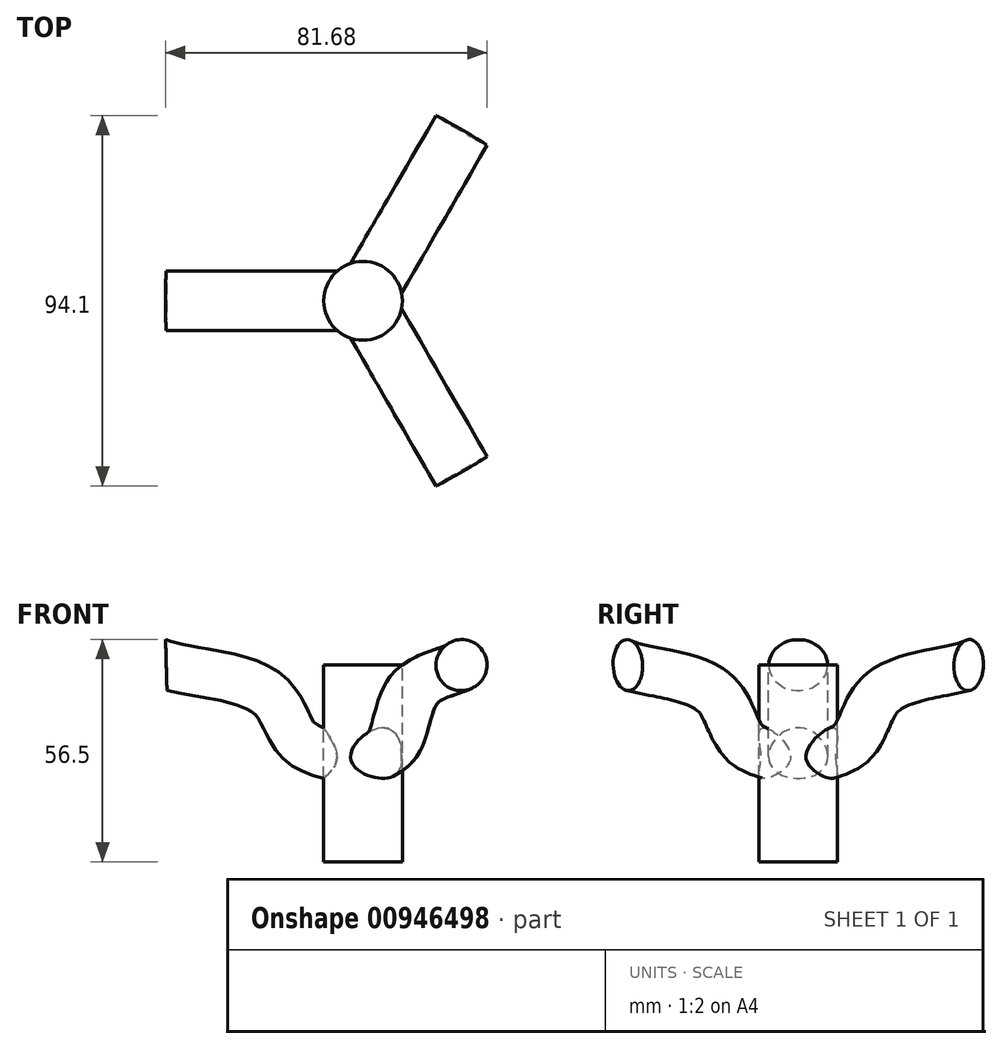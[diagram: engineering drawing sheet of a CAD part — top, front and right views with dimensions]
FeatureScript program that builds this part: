
annotation { "Feature Type Name" : "Feature", "Feature Type Description" : "" }
export const myFeature = defineFeature(function(context is Context, id is Id, definition is map)
    precondition{}
    {
        {
            var Q0;
            Q0=qCreatedBy(makeId("Front.planeOp"),FACE);
            var sketch = newSketch(context, id + "F0", { "sketchPlane" : qUnion([Q0])});
            skLineSegment(sketch, "E0", {"start": v(0, 75.01) * mm, "end": v(0, -75) * mm});
            skSolve(sketch);
        }
        {
            var Q0;
            Q0=qCreatedBy(makeId("Front.planeOp"),FACE);
            var sketch = newSketch(context, id + "F1", { "sketchPlane" : qUnion([Q0])});
            skCircle(sketch, "E1", {"center": v(-50, 0) * mm, "radius": 7.5 * mm});
            skSolve(sketch);
        }
        {
            var Q0;
            Q0=sQuery(id+"F1.wireOp",EDGE,"E1");
            var Q1;
            Q1=sQuery(id+"F0.wireOp",EDGE,"E0");
            revolve(context, id + "F2", {"bodyType" : ToolBodyType.SURFACE, "surfaceOperationType" : NewSurfaceOperationType.NEW, "surfaceEntities" : qUnion([Q0]), "axis" : qUnion([Q1]), "revolveType" : RevolveType.FULL});
        }
        {
            var Q0;
            Q0=qCreatedBy(makeId("Top.planeOp"),FACE);
            var sketch = newSketch(context, id + "F3", { "sketchPlane" : qUnion([Q0])});
            skCircle(sketch, "E2", {"center": v(0, 0) * mm, "radius": 10 * mm});
            skSolve(sketch);
        }
        {
            var Q0;
            Q0=makeQuery(id+"F3.imprint","IMPRINT",FACE,{"disambiguationData":[TD([[makeQuery(id+"F3.imprint","IMPRINT",EDGE,{"derivedFrom":sQuery(id+"F3.wireOp",EDGE,"E2")}),1.0]])]});
            var Q1;
            Q1=sQuery(id+"F3.wireOp",EDGE,"E2");
            extrude(context, id + "F4", {"entities" : qUnion([Q0]), "surfaceEntities" : qUnion([Q1]), "oppositeDirection" : true, "depth" : 50 * mm, "offsetDistance" : 25 * mm});
        }
        {
            var Q0;
            Q0=qCreatedBy(makeId("Front.planeOp"),FACE);
            var sketch = newSketch(context, id + "F5", { "sketchPlane" : qUnion([Q0])});
            skFitSpline(sketch, "E3", {"points": [v(0, -25) * mm, v(-15.64, -19.5) * mm, v(-25, -6.91) * mm, v(-50, 0) * mm], "startDerivative": vector(-47.32, 16.36) * mm, "endDerivative": vector(-48.49, 15.27) * mm});
            skSolve(sketch);
        }
        {
            var Q0;
            Q0=qCreatedBy(makeId("Right.planeOp"),FACE);
            var sketch = newSketch(context, id + "F6", { "sketchPlane" : qUnion([Q0])});
            skEllipse(sketch, "E4", {"center": v(0, -25) * mm, "majorRadius": 6.5 * mm, "minorRadius": 7.5 * mm, "majorAxis": v(0, 1)});
            skSolve(sketch);
        }
        {
            var Q0;
            Q0 = qSketchRegion(id + "F6", true);
            var Q1;
            Q1 = qConstructionFilter(qBodyType(qCreatedBy(id + "F5" ,EDGE), BodyType.WIRE), ConstructionObject.NO);
            sweep(context, id + "F7", {"operationType" : NewBodyOperationType.ADD, "profiles" : qUnion([Q0]), "path" : qUnion([Q1])});
        }
        {
            var Q0;
            Q0=makeQuery(id+"F4.opExtrude","SWEPT_BODY",BODY,{"disambiguationData":[OSD([sQuery(id+"F3.wireOp",EDGE,"E2")])]});
            var Q1;
            Q1=makeQuery(id+"F4.opExtrude","SWEPT_FACE",FACE,{"disambiguationData":[OSD([sQuery(id+"F3.wireOp",EDGE,"E2")])]});
            circularPattern(context, id + "F8", {"entities" : qUnion([Q0]), "axis" : qUnion([Q1]), "angle" : 360 * degree, "instanceCount" : 3, "equalSpace" : true});
        }
    });
